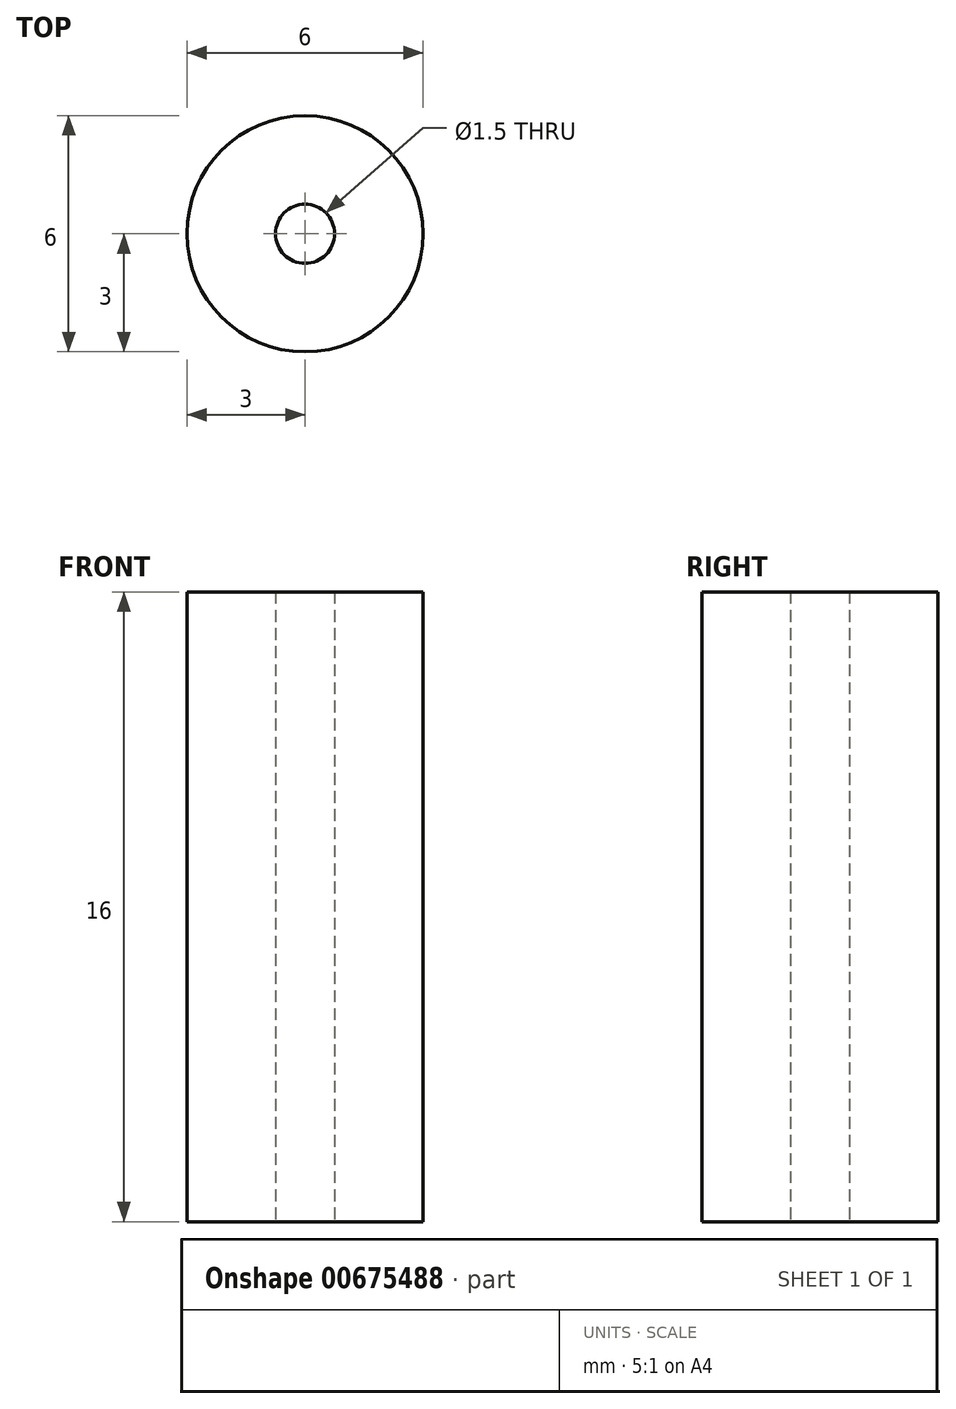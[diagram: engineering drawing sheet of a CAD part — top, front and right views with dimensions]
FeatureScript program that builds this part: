
annotation { "Feature Type Name" : "Feature", "Feature Type Description" : "" }
export const myFeature = defineFeature(function(context is Context, id is Id, definition is map)
    precondition{}
    {
        {
            var Q0;
            Q0=qCreatedBy(makeId("Top.planeOp"),FACE);
            var sketch = newSketch(context, id + "F0", { "sketchPlane" : qUnion([Q0])});
            skCircle(sketch, "E0", {"center": v(0, 0) * mm, "radius": 3 * mm});
            skCircle(sketch, "E1", {"center": v(0, 0) * mm, "radius": 0.75 * mm});
            skSolve(sketch);
        }
        {
            var Q0;
            Q0=makeQuery(id+"F0.imprint","IMPRINT",FACE,{"disambiguationData":[TD([[makeQuery(id+"F0.imprint","IMPRINT",EDGE,{"derivedFrom":sQuery(id+"F0.wireOp",EDGE,"E0")}),1.0]])]});
            extrude(context, id + "F1", {"entities" : qUnion([Q0]), "depth" : 16 * mm, "offsetDistance" : 25 * mm});
        }
    });
